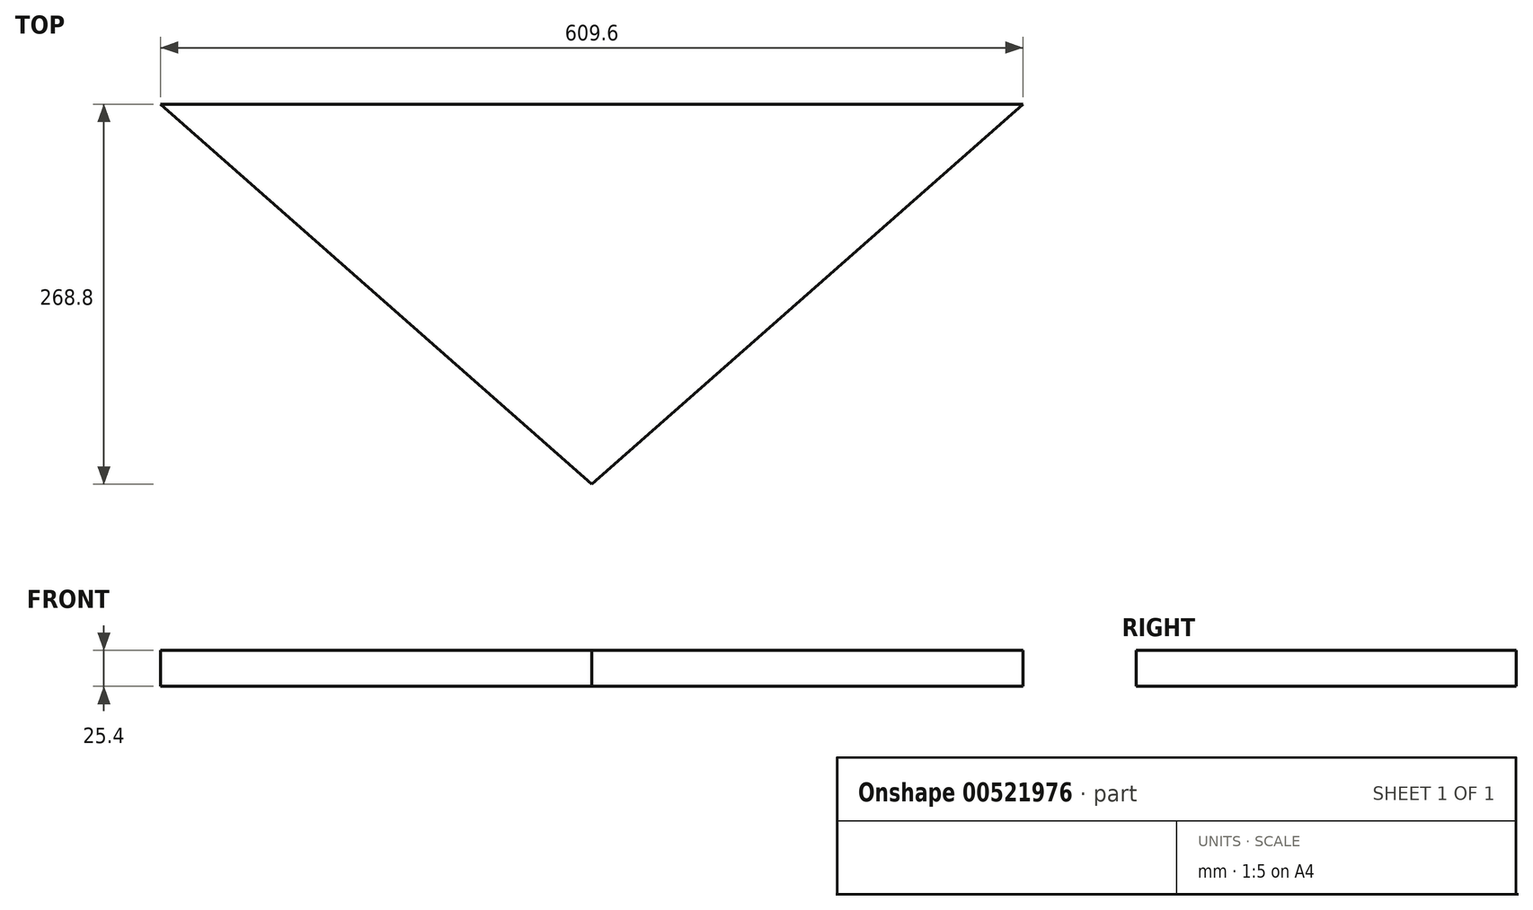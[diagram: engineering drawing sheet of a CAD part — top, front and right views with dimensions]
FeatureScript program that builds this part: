
annotation { "Feature Type Name" : "Feature", "Feature Type Description" : "" }
export const myFeature = defineFeature(function(context is Context, id is Id, definition is map)
    precondition{}
    {
        {
            var Q0;
            Q0=qCreatedBy(makeId("Top.planeOp"),FACE);
            var sketch = newSketch(context, id + "F0", { "sketchPlane" : qUnion([Q0])});
            skLineSegment(sketch, "E0", {"start": v(-302.23, 307.17) * mm, "end": v(307.37, 307.17) * mm});
            skLineSegment(sketch, "E1", {"start": v(307.37, 307.17) * mm, "end": v(2.57, 38.37) * mm});
            skLineSegment(sketch, "E2", {"start": v(2.57, 38.37) * mm, "end": v(-302.23, 307.17) * mm});
            skSolve(sketch);
        }
        {
            var Q0;
            Q0 = qSketchRegion(id + "F0", true);
            var Q1;
            Q1 = qBodyType(qCreatedBy(id + "F0" ,EDGE), BodyType.WIRE);
            extrude(context, id + "F1", {"entities" : qUnion([Q0]), "surfaceEntities" : qUnion([Q1]), "depth" : 25.4 * mm, "offsetDistance" : 25.4 * mm});
        }
    });
